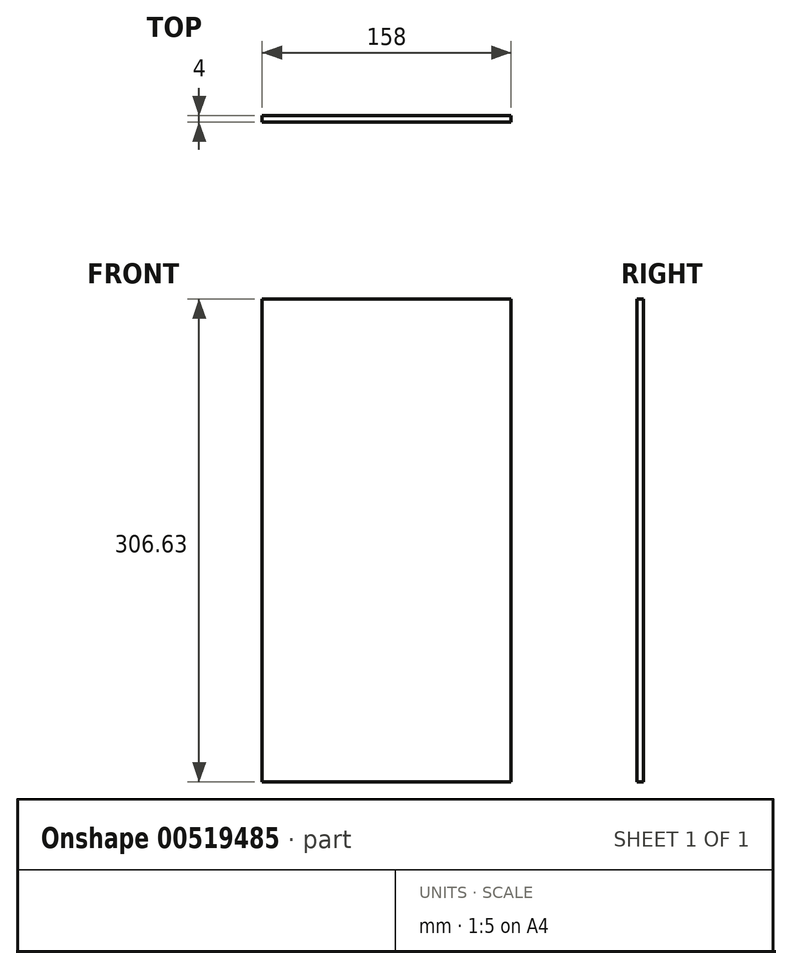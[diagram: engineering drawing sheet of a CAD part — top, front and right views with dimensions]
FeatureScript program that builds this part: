
annotation { "Feature Type Name" : "Feature", "Feature Type Description" : "" }
export const myFeature = defineFeature(function(context is Context, id is Id, definition is map)
    precondition{}
    {
        {
            var Q0;
            Q0=qCreatedBy(makeId("Front.planeOp"),FACE);
            var sketch = newSketch(context, id + "F0", { "sketchPlane" : qUnion([Q0])});
            skLineSegment(sketch, "E0.bottom", {"start": v(0, 0) * mm, "end": v(158, 0) * mm});
            skLineSegment(sketch, "E0.top", {"start": v(0, 306.63) * mm, "end": v(158, 306.63) * mm});
            skLineSegment(sketch, "E0.left", {"start": v(0, 0) * mm, "end": v(0, 306.63) * mm});
            skLineSegment(sketch, "E0.right", {"start": v(158, 0) * mm, "end": v(158, 306.63) * mm});
            skSolve(sketch);
        }
        {
            var Q0;
            Q0=makeQuery(id+"F0.imprint","IMPRINT",FACE,{"disambiguationData":[TD([[makeQuery(id+"F0.imprint","IMPRINT",EDGE,{"derivedFrom":sQuery(id+"F0.wireOp",EDGE,"E0.bottom")}),1.0]])]});
            extrude(context, id + "F1", {"entities" : qUnion([Q0]), "depth" : 4 * mm, "offsetDistance" : 25 * mm});
        }
    });
